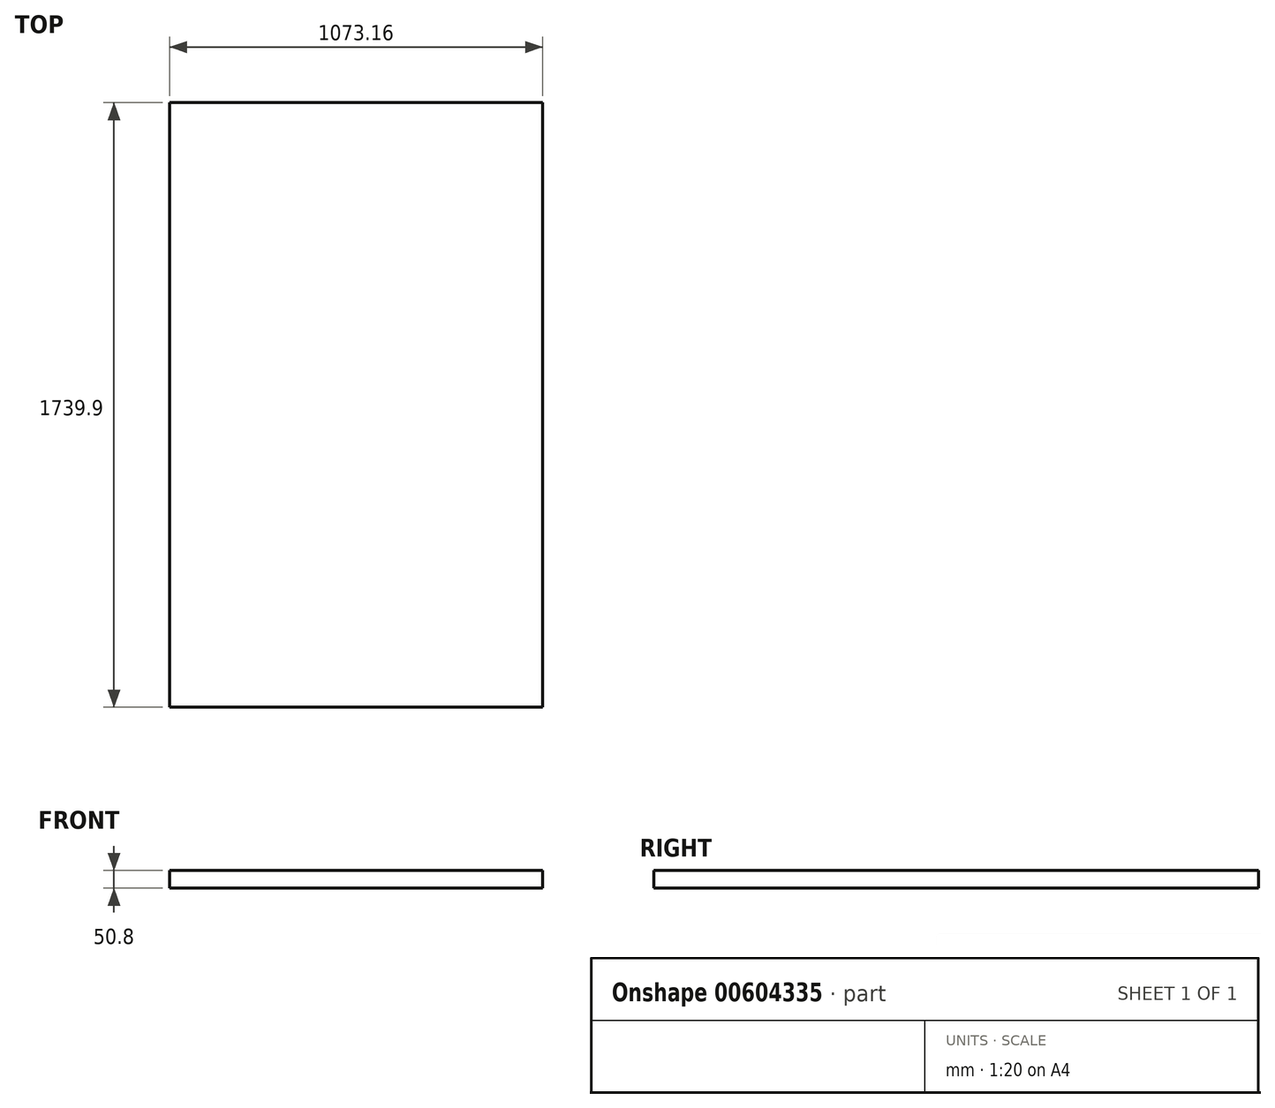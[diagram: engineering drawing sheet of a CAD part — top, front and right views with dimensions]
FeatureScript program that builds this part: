
annotation { "Feature Type Name" : "Feature", "Feature Type Description" : "" }
export const myFeature = defineFeature(function(context is Context, id is Id, definition is map)
    precondition{}
    {
        {
            var Q0;
            Q0=qCreatedBy(makeId("Top.planeOp"),FACE);
            var sketch = newSketch(context, id + "F0", { "sketchPlane" : qUnion([Q0])});
            skLineSegment(sketch, "E0.bottom", {"start": v(536.58, 869.95) * mm, "end": v(-536.57, 869.95) * mm});
            skLineSegment(sketch, "E0.top", {"start": v(536.57, -869.95) * mm, "end": v(-536.58, -869.95) * mm});
            skLineSegment(sketch, "E0.left", {"start": v(536.58, 869.95) * mm, "end": v(536.57, -869.95) * mm});
            skLineSegment(sketch, "E0.right", {"start": v(-536.57, 869.95) * mm, "end": v(-536.58, -869.95) * mm});
            skPoint(sketch, "E0.middle", {"position": v(0, 0) * mm});
            skSolve(sketch);
        }
        {
            var Q0;
            Q0=makeQuery(id+"F0.imprint","IMPRINT",FACE,{"disambiguationData":[TD([[makeQuery(id+"F0.imprint","IMPRINT",EDGE,{"derivedFrom":sQuery(id+"F0.wireOp",EDGE,"E0.bottom")}),1.0]])]});
            extrude(context, id + "F1", {"entities" : qUnion([Q0]), "depth" : 50.8 * mm, "offsetDistance" : 25.4 * mm});
        }
    });
